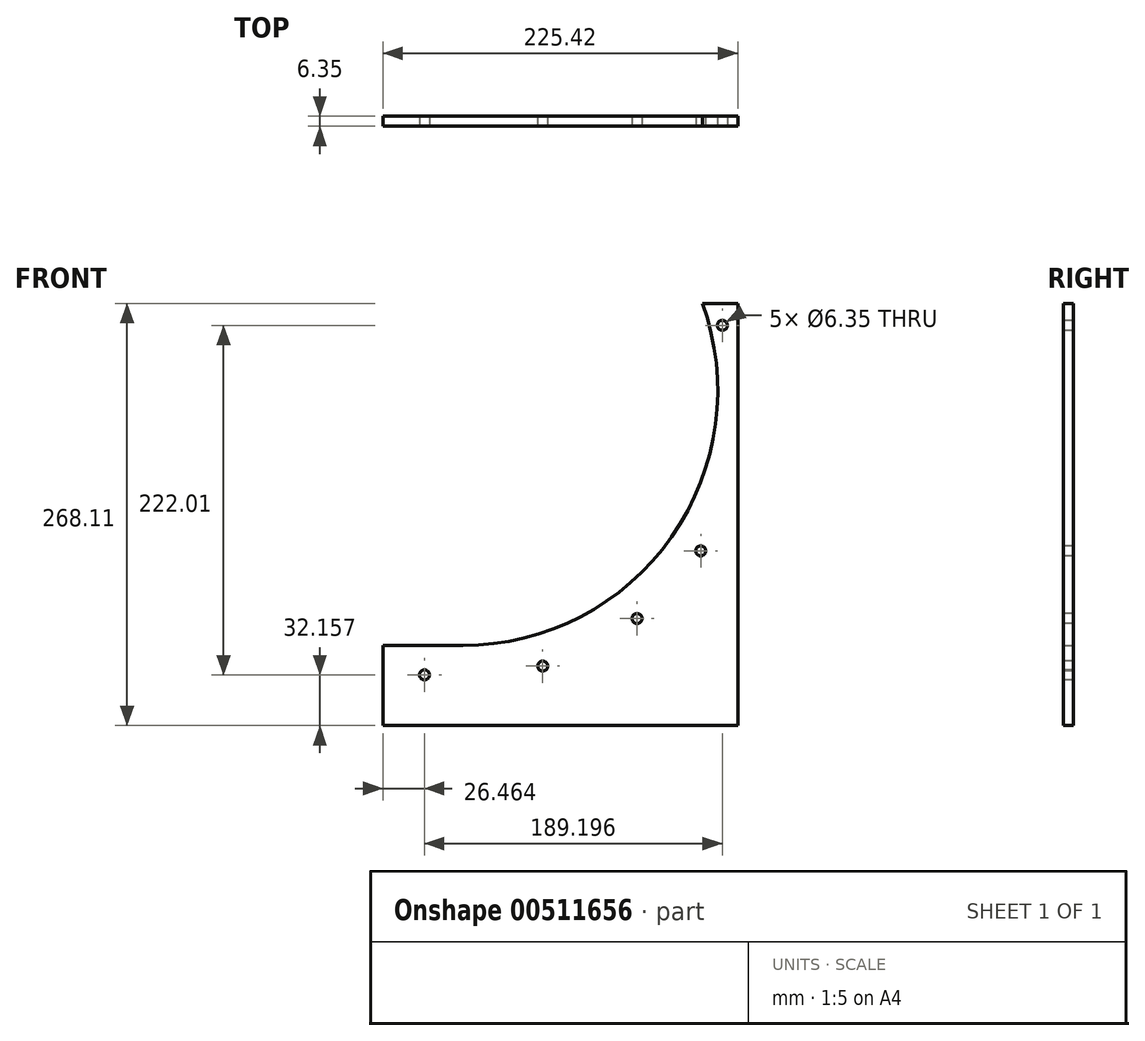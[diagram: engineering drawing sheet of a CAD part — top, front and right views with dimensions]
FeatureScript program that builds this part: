
annotation { "Feature Type Name" : "Feature", "Feature Type Description" : "" }
export const myFeature = defineFeature(function(context is Context, id is Id, definition is map)
    precondition{}
    {
        {
            var Q0;
            Q0=qCreatedBy(makeId("Front.planeOp"),FACE);
            var sketch = newSketch(context, id + "F0", { "sketchPlane" : qUnion([Q0])});
            skLineSegment(sketch, "E0", {"start": v(0, 0) * mm, "end": v(174.62, 0) * mm});
            skLineSegment(sketch, "E1", {"start": v(174.62, 0) * mm, "end": v(174.62, 268.1) * mm});
            skLineSegment(sketch, "E2", {"start": v(174.62, 268.1) * mm, "end": v(152.16, 268.1) * mm});
            skLineSegment(sketch, "E3", {"start": v(0, 0) * mm, "end": v(0, 50.8) * mm});
            skArc(sketch, "E4", {"start": v(0, 50.8) * mm, "mid": v(132.64, 119.85) * mm, "end": v(152.16, 268.1) * mm});
            skLineSegment(sketch, "E5", {"start": v(0, 212.73) * mm, "end": v(152.16, 268.1) * mm, "construction": true});
            skLineSegment(sketch, "E6", {"start": v(0, 212.73) * mm, "end": v(161.93, 212.73) * mm, "construction": true});
            skLineSegment(sketch, "E7.bottom", {"start": v(0, 50.8) * mm, "end": v(-50.8, 50.8) * mm});
            skLineSegment(sketch, "E7.top", {"start": v(0, 0) * mm, "end": v(-50.8, 0) * mm});
            skLineSegment(sketch, "E7.left", {"start": v(0, 50.8) * mm, "end": v(0, 0) * mm});
            skLineSegment(sketch, "E7.right", {"start": v(-50.8, 50.8) * mm, "end": v(-50.8, 0) * mm});
            skSolve(sketch);
        }
        {
            var Q0;
            Q0=makeQuery(id+"F0.imprint","IMPRINT",FACE,{"disambiguationData":[TD([[makeQuery(id+"F0.imprint","IMPRINT",EDGE,{"derivedFrom":sQuery(id+"F0.wireOp",EDGE,"E0")}),1.0]])]});
            var Q1;
            Q1=makeQuery(id+"F0.imprint","IMPRINT",FACE,{"disambiguationData":[TD([[makeQuery(id+"F0.imprint","IMPRINT",EDGE,{"derivedFrom":sQuery(id+"F0.wireOp",EDGE,"E7.bottom")}),1.0]])]});
            extrude(context, id + "F1", {"entities" : qUnion([Q0, Q1]), "depth" : 6.35 * mm, "offsetDistance" : 25.4 * mm});
        }
        {
            var Q0;
            Q0=makeQuery(id+"F1.opExtrude","CAP_FACE",FACE,{"disambiguationData":[OSD([sQuery(id+"F0.wireOp",EDGE,"E0"),sQuery(id+"F0.wireOp",EDGE,"E1"),sQuery(id+"F0.wireOp",EDGE,"E2"),sQuery(id+"F0.wireOp",EDGE,"E4"),sQuery(id+"F0.wireOp",EDGE,"E7.bottom"),sQuery(id+"F0.wireOp",EDGE,"E7.top"),sQuery(id+"F0.wireOp",EDGE,"E7.right")])],"isStart":false});
            var sketch = newSketch(context, id + "F2", { "sketchPlane" : qUnion([Q0])});
            skCircle(sketch, "E8", {"center": v(-24.34, 32.16) * mm, "radius": 3.18 * mm});
            skCircle(sketch, "E9", {"center": v(50.78, 37.74) * mm, "radius": 3.18 * mm});
            skCircle(sketch, "E10", {"center": v(110.65, 67.97) * mm, "radius": 3.18 * mm});
            skCircle(sketch, "E11", {"center": v(151.12, 110.94) * mm, "radius": 3.18 * mm});
            skCircle(sketch, "E12", {"center": v(164.86, 254.17) * mm, "radius": 3.18 * mm});
            skCircle(sketch, "E13", {"center": v(0, 212.73) * mm, "radius": 182.2 * mm, "construction": true});
            skSolve(sketch);
        }
        {
            var Q0;
            Q0=makeQuery(id+"F2.imprint","IMPRINT",FACE,{"disambiguationData":[TD([[makeQuery(id+"F2.imprint","IMPRINT",EDGE,{"derivedFrom":sQuery(id+"F2.wireOp",EDGE,"E8")}),1.0]])]});
            var Q1;
            Q1=makeQuery(id+"F2.imprint","IMPRINT",FACE,{"disambiguationData":[TD([[makeQuery(id+"F2.imprint","IMPRINT",EDGE,{"derivedFrom":sQuery(id+"F2.wireOp",EDGE,"E9")}),1.0]])]});
            var Q2;
            Q2=makeQuery(id+"F2.imprint","IMPRINT",FACE,{"disambiguationData":[TD([[makeQuery(id+"F2.imprint","IMPRINT",EDGE,{"derivedFrom":sQuery(id+"F2.wireOp",EDGE,"E10")}),1.0]])]});
            var Q3;
            Q3=makeQuery(id+"F2.imprint","IMPRINT",FACE,{"disambiguationData":[TD([[makeQuery(id+"F2.imprint","IMPRINT",EDGE,{"derivedFrom":sQuery(id+"F2.wireOp",EDGE,"E11")}),1.0]])]});
            var Q4;
            Q4=makeQuery(id+"F2.imprint","IMPRINT",FACE,{"disambiguationData":[TD([[makeQuery(id+"F2.imprint","IMPRINT",EDGE,{"derivedFrom":sQuery(id+"F2.wireOp",EDGE,"E12")}),1.0]])]});
            extrude(context, id + "F3", {"entities" : qUnion([Q0, Q1, Q2, Q3, Q4]), "operationType" : NewBodyOperationType.REMOVE, "oppositeDirection" : true, "depth" : 25.4 * mm, "offsetDistance" : 25.4 * mm});
        }
    });
